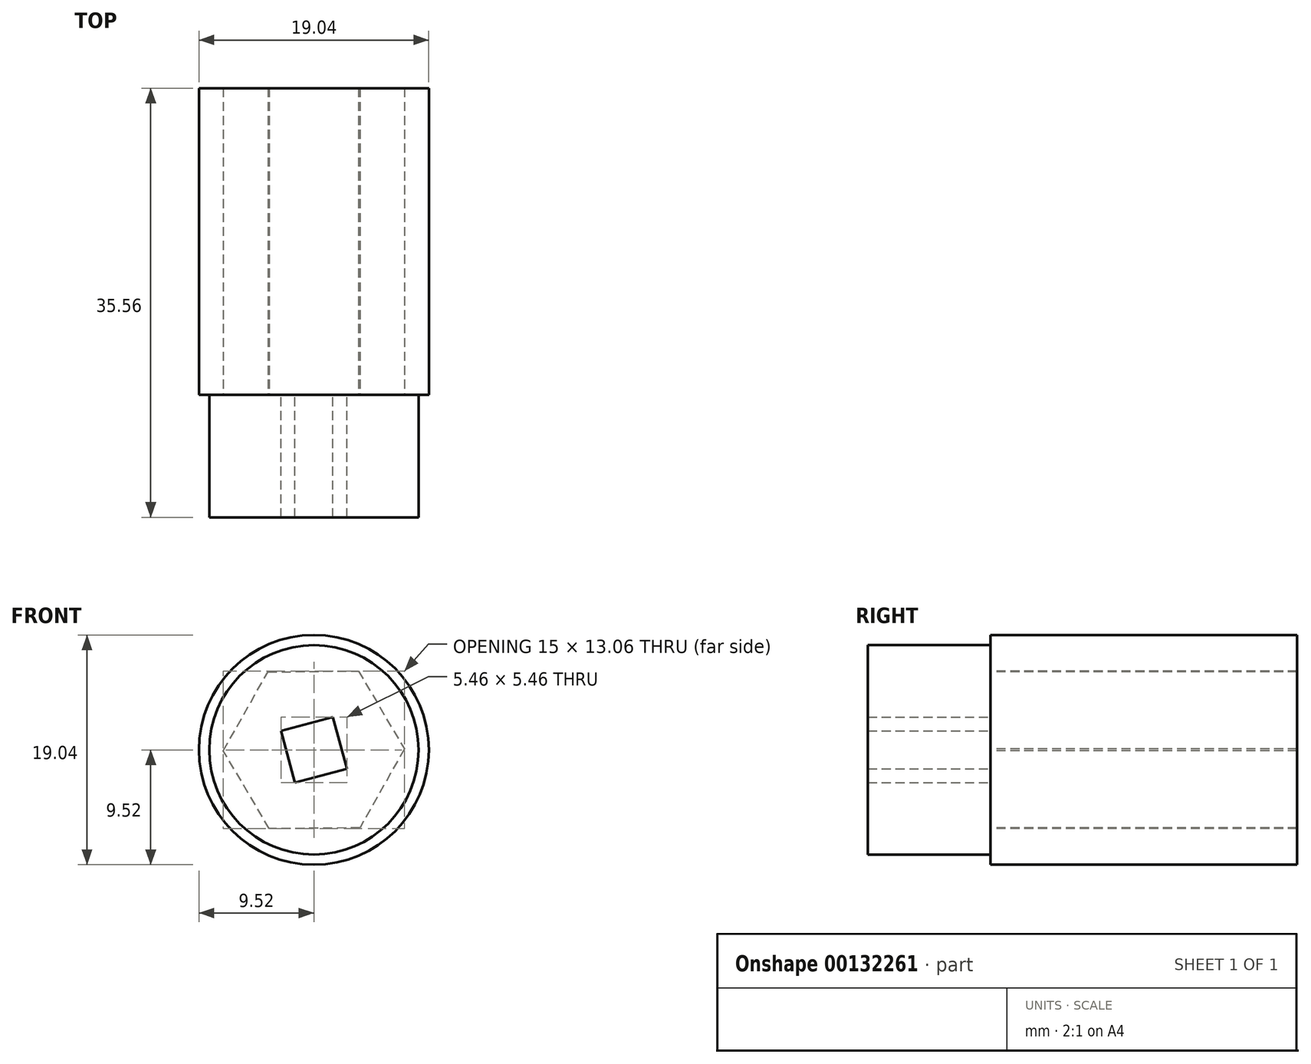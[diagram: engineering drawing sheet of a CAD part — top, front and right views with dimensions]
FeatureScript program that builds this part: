
annotation { "Feature Type Name" : "Feature", "Feature Type Description" : "" }
export const myFeature = defineFeature(function(context is Context, id is Id, definition is map)
    precondition{}
    {
        {
            var Q0;
            Q0=qCreatedBy(makeId("Front.planeOp"),FACE);
            var sketch = newSketch(context, id + "F0", { "sketchPlane" : qUnion([Q0])});
            skLineSegment(sketch, "E0.0", {"start": v(1.58, 2.73) * mm, "end": v(2.73, -1.58) * mm});
            skLineSegment(sketch, "E0.1", {"start": v(2.73, -1.58) * mm, "end": v(-1.58, -2.73) * mm});
            skLineSegment(sketch, "E0.2", {"start": v(-1.58, -2.73) * mm, "end": v(-2.73, 1.58) * mm});
            skLineSegment(sketch, "E0.3", {"start": v(-2.73, 1.58) * mm, "end": v(1.58, 2.73) * mm});
            skLineSegment(sketch, "E1", {"start": v(1.58, 2.73) * mm, "end": v(-1.58, -2.73) * mm});
            skCircle(sketch, "E2", {"center": v(0, 0) * mm, "radius": 8.67 * mm});
            skSolve(sketch);
        }
        {
            var Q0;
            Q0 = qSketchRegion(id + "F0", true);
            extrude(context, id + "F1", {"entities" : qUnion([Q0]), "depth" : 10.16 * mm});
        }
        {
            var Q0;
            Q0=qCreatedBy(makeId("Front.planeOp"),FACE);
            var sketch = newSketch(context, id + "F2", { "sketchPlane" : qUnion([Q0])});
            skLineSegment(sketch, "E3.0", {"start": v(-3.81, 6.46) * mm, "end": v(3.69, 6.53) * mm});
            skLineSegment(sketch, "E3.1", {"start": v(3.69, 6.53) * mm, "end": v(7.5, 0.07) * mm});
            skLineSegment(sketch, "E3.2", {"start": v(7.5, 0.07) * mm, "end": v(3.81, -6.46) * mm});
            skLineSegment(sketch, "E3.3", {"start": v(3.81, -6.46) * mm, "end": v(-3.69, -6.53) * mm});
            skLineSegment(sketch, "E3.4", {"start": v(-3.69, -6.53) * mm, "end": v(-7.5, -0.07) * mm});
            skLineSegment(sketch, "E3.5", {"start": v(-7.5, -0.07) * mm, "end": v(-3.81, 6.46) * mm});
            skLineSegment(sketch, "E4", {"start": v(-3.81, 6.46) * mm, "end": v(3.81, -6.46) * mm});
            skCircle(sketch, "E5", {"center": v(0, 0) * mm, "radius": 9.52 * mm});
            skSolve(sketch);
        }
        {
            var Q0;
            Q0=makeQuery(id+"F2.imprint","IMPRINT",FACE,{"disambiguationData":[TD([[makeQuery(id+"F2.imprint","IMPRINT",EDGE,{"derivedFrom":sQuery(id+"F2.wireOp",EDGE,"E3.0")}),1.0]])]});
            extrude(context, id + "F3", {"entities" : qUnion([Q0]), "oppositeDirection" : true, "depth" : 25.4 * mm});
        }
    });
